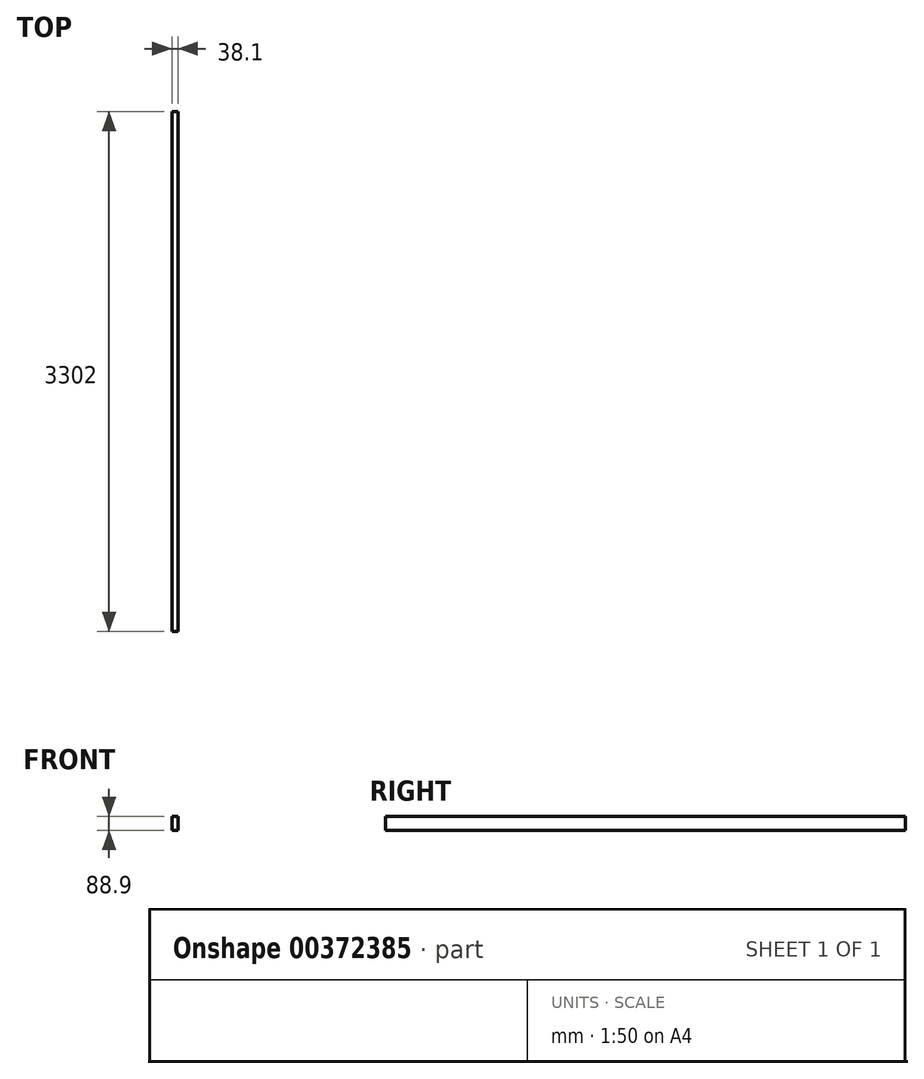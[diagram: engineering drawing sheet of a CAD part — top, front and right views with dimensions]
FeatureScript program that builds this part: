
annotation { "Feature Type Name" : "Feature", "Feature Type Description" : "" }
export const myFeature = defineFeature(function(context is Context, id is Id, definition is map)
    precondition{}
    {
        {
            var Q0;
            Q0=qCreatedBy(makeId("Front.planeOp"),FACE);
            var sketch = newSketch(context, id + "F0", { "sketchPlane" : qUnion([Q0])});
            skLineSegment(sketch, "E0.bottom", {"start": v(-19.05, 44.45) * mm, "end": v(19.05, 44.45) * mm});
            skLineSegment(sketch, "E0.top", {"start": v(-19.05, -44.45) * mm, "end": v(19.05, -44.45) * mm});
            skLineSegment(sketch, "E0.left", {"start": v(-19.05, 44.45) * mm, "end": v(-19.05, -44.45) * mm});
            skLineSegment(sketch, "E0.right", {"start": v(19.05, 44.45) * mm, "end": v(19.05, -44.45) * mm});
            skPoint(sketch, "E0.middle", {"position": v(0, 0) * mm});
            skSolve(sketch);
        }
        {
            var Q0;
            Q0=qSketchRegion(id+"F0",true);
            extrude(context, id + "F1", {"entities" : qUnion([Q0]), "endBound" : BoundingType.SYMMETRIC, "oppositeDirection" : true, "depth" : 3302 * mm});
        }
    });
